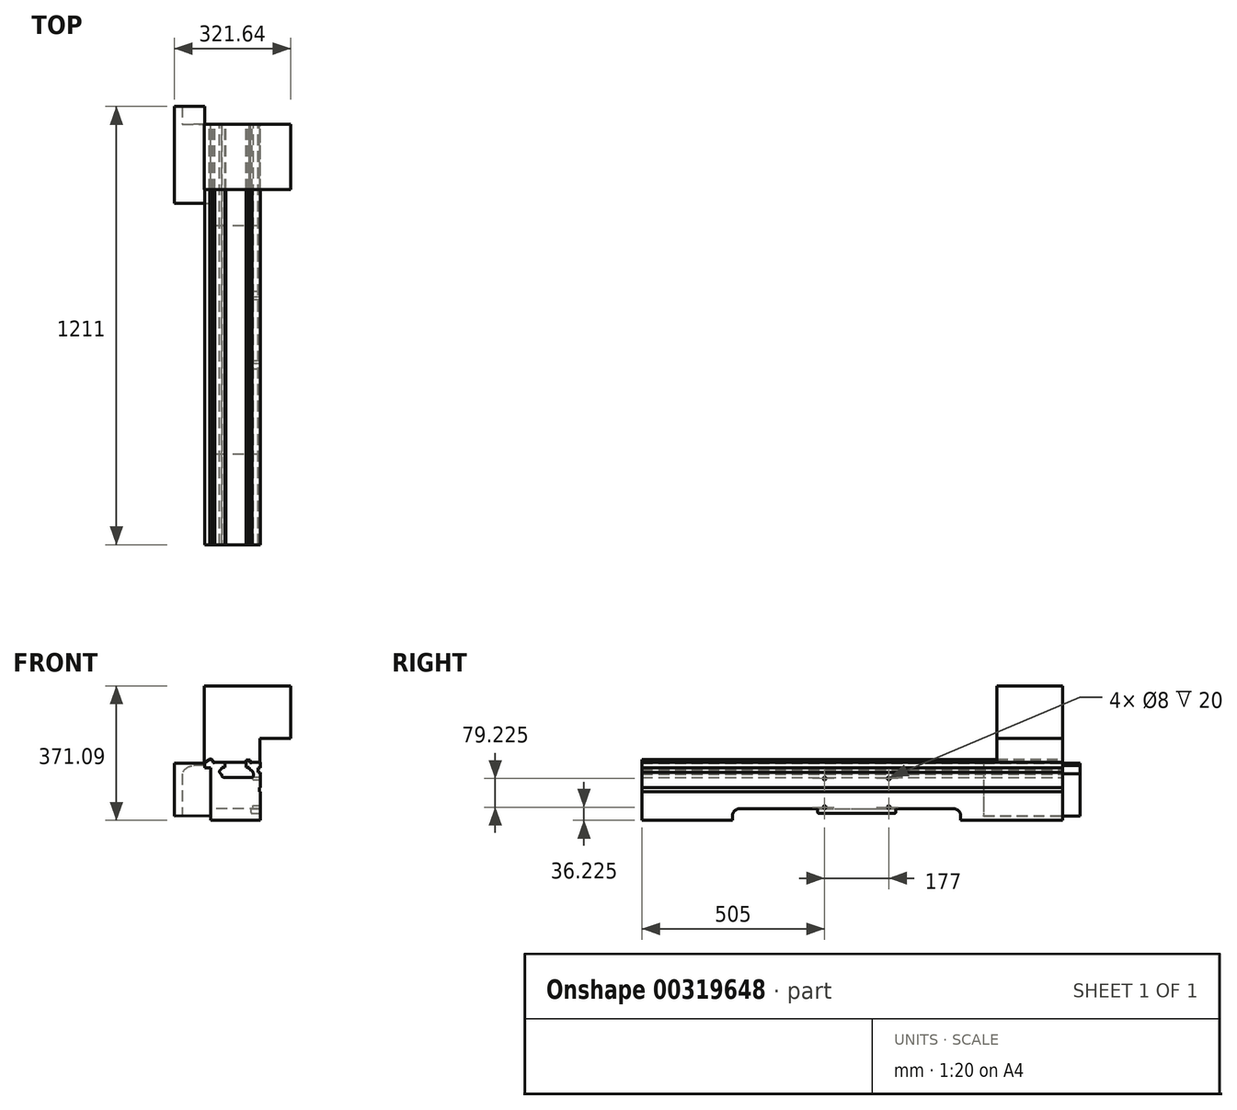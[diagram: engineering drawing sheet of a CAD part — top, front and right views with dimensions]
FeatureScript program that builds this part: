
annotation { "Feature Type Name" : "Feature", "Feature Type Description" : "" }
export const myFeature = defineFeature(function(context is Context, id is Id, definition is map)
    precondition{}
    {
        {
            var Q0;
            Q0=qCreatedBy(makeId("Front.planeOp"),FACE);
            var sketch = newSketch(context, id + "F0", { "sketchPlane" : qUnion([Q0])});
            skLineSegment(sketch, "E0", {"start": v(0, 0) * mm, "end": v(98, 0) * mm, "construction": true});
            skLineSegment(sketch, "E1", {"start": v(98, 0) * mm, "end": v(98, -15) * mm});
            skLineSegment(sketch, "E2", {"start": v(0, 0) * mm, "end": v(0, -14.5) * mm});
            skLineSegment(sketch, "E3", {"start": v(98, 0) * mm, "end": v(74.8, 0) * mm});
            skLineSegment(sketch, "E4", {"start": v(0, 0) * mm, "end": v(-27.25, 0) * mm});
            skLineSegment(sketch, "E5", {"start": v(0, 0) * mm, "end": v(-33, 0) * mm, "construction": true});
            skLineSegment(sketch, "E6.0", {"start": v(-33, -1.5) * mm, "end": v(98, -1.5) * mm, "construction": true});
            skLineSegment(sketch, "E7", {"start": v(-33, -1.5) * mm, "end": v(-33, 2) * mm});
            skLineSegment(sketch, "E8", {"start": v(-33, -1.5) * mm, "end": v(-29, -1.5) * mm});
            skLineSegment(sketch, "E9", {"start": v(98, -15) * mm, "end": v(58, -15) * mm, "construction": true});
            skLineSegment(sketch, "E10", {"start": v(0, -14.5) * mm, "end": v(-9, -14.5) * mm});
            skLineSegment(sketch, "E11", {"start": v(-9, -14.5) * mm, "end": v(-9, -19) * mm});
            skLineSegment(sketch, "E12", {"start": v(-27.25, 0) * mm, "end": v(-29, -1.5) * mm});
            skLineSegment(sketch, "E13", {"start": v(-33, 2) * mm, "end": v(-37.4, 7.44) * mm});
            skLineSegment(sketch, "E14", {"start": v(-37.4, 7.44) * mm, "end": v(-42.4, 7.44) * mm});
            skLineSegment(sketch, "E15", {"start": v(-42.4, 7.44) * mm, "end": v(-56.42, -2.19) * mm});
            skLineSegment(sketch, "E16", {"start": v(-56.42, -2.19) * mm, "end": v(-56.42, -15.19) * mm});
            skLineSegment(sketch, "E17", {"start": v(-56.42, -15.19) * mm, "end": v(-38.92, -15.19) * mm});
            skLineSegment(sketch, "E18", {"start": v(-38.92, -15.19) * mm, "end": v(-38.92, -97.19) * mm});
            skLineSegment(sketch, "E19", {"start": v(0, -14.5) * mm, "end": v(58, -14.5) * mm, "construction": true});
            skLineSegment(sketch, "E20", {"start": v(98, -15) * mm, "end": v(91.2, -15) * mm});
            skLineSegment(sketch, "E21", {"start": v(91.2, -15) * mm, "end": v(91.2, -28) * mm});
            skLineSegment(sketch, "E22", {"start": v(91.2, -28) * mm, "end": v(98, -28) * mm});
            skLineSegment(sketch, "E23", {"start": v(98, -28) * mm, "end": v(98, -70.45) * mm});
            skLineSegment(sketch, "E24", {"start": v(98, -70.45) * mm, "end": v(95.75, -70.45) * mm});
            skLineSegment(sketch, "E25", {"start": v(95.75, -70.45) * mm, "end": v(95.75, -80.95) * mm});
            skLineSegment(sketch, "E26", {"start": v(95.75, -80.95) * mm, "end": v(98, -80.95) * mm});
            skLineSegment(sketch, "E27", {"start": v(98, -80.95) * mm, "end": v(98, -160.45) * mm});
            skLineSegment(sketch, "E28", {"start": v(98, -160.45) * mm, "end": v(-38.92, -160.45) * mm});
            skLineSegment(sketch, "E29", {"start": v(-38.92, -160.45) * mm, "end": v(-38.92, -97.19) * mm});
            skLineSegment(sketch, "E30", {"start": v(68.7, -1.5) * mm, "end": v(68.7, 1) * mm});
            skLineSegment(sketch, "E31", {"start": v(68.7, -1.5) * mm, "end": v(72.95, -1.5) * mm});
            skLineSegment(sketch, "E32", {"start": v(72.95, -1.5) * mm, "end": v(74.8, 0) * mm});
            skLineSegment(sketch, "E33", {"start": v(68.7, 1) * mm, "end": v(65.56, 4.5) * mm});
            skLineSegment(sketch, "E34", {"start": v(65.56, 4.5) * mm, "end": v(61.71, 4.5) * mm});
            skLineSegment(sketch, "E35", {"start": v(61.71, 4.5) * mm, "end": v(58, 0.65) * mm});
            skLineSegment(sketch, "E36", {"start": v(58, 0.65) * mm, "end": v(58, -14.55) * mm});
            skLineSegment(sketch, "E37", {"start": v(58, -14.5) * mm, "end": v(68, -14.5) * mm});
            skLineSegment(sketch, "E38", {"start": v(68, -14.5) * mm, "end": v(68, -20.75) * mm});
            skLineSegment(sketch, "E39", {"start": v(2.3, -42) * mm, "end": v(71.25, -42) * mm});
            skArc(sketch, "E40", {"start": v(-9, -19) * mm, "mid": v(-15.02, -25.93) * mm, "end": v(-9, -32.86) * mm});
            skFitSpline(sketch, "E41", {"points": [v(-9, -32.86) * mm, v(-9, -37.28) * mm, v(-6.71, -40.5) * mm, v(-2.73, -41.64) * mm, v(0, -41.91) * mm, v(2.3, -42) * mm], "startDerivative": vector(-2.55, -20.76) * mm, "endDerivative": vector(16.47, -0.8) * mm});
            skFitSpline(sketch, "E42", {"points": [v(68, -20.75) * mm, v(72.98, -22.15) * mm, v(76.39, -26.46) * mm, v(78.72, -32.74) * mm, v(78.9, -37.4) * mm, v(77.64, -39.92) * mm, v(74.36, -41.44) * mm, v(71.25, -42) * mm], "startDerivative": vector(34.62, -4.93) * mm, "endDerivative": vector(-31.04, -3.2) * mm});
            skSolve(sketch);
        }
        {
            var Q0;
            Q0=makeQuery(id+"F0.imprint","IMPRINT",FACE,{"disambiguationData":[TD([[makeQuery(id+"F0.imprint","IMPRINT",EDGE,{"derivedFrom":sQuery(id+"F0.wireOp",EDGE,"E1")}),-1.0]])]});
            extrude(context, id + "F1", {"entities" : qUnion([Q0]), "depth" : 1162 * mm});
        }
        {
            var Q0;
            Q0=makeQuery(id+"F1.opExtrude","SWEPT_FACE",FACE,{"disambiguationData":[OSD([sQuery(id+"F0.wireOp",EDGE,"E18"),sQuery(id+"F0.wireOp",EDGE,"E29")])]});
            var sketch = newSketch(context, id + "F2", { "sketchPlane" : qUnion([Q0])});
            skLineSegment(sketch, "E43", {"start": v(1162, -160.45) * mm, "end": v(912, -160.45) * mm, "construction": true});
            skLineSegment(sketch, "E44", {"start": v(0, -160.45) * mm, "end": v(281, -160.45) * mm, "construction": true});
            skLineSegment(sketch, "E45", {"start": v(912, -160.45) * mm, "end": v(912, -148.45) * mm});
            skLineSegment(sketch, "E46", {"start": v(892, -128.45) * mm, "end": v(301, -128.45) * mm});
            skLineSegment(sketch, "E47", {"start": v(281, -148.45) * mm, "end": v(281, -160.45) * mm});
            skLineSegment(sketch, "E48", {"start": v(281, -160.45) * mm, "end": v(912, -160.45) * mm});
            skPoint(sketch, "E49.visualSharp", {"position": v(281, -128.45) * mm});
            skArc(sketch, "E49.filletArc", {"start": v(301, -128.45) * mm, "mid": v(286.86, -134.3) * mm, "end": v(281, -148.45) * mm});
            skPoint(sketch, "E50.visualSharp", {"position": v(912, -128.45) * mm});
            skArc(sketch, "E50.filletArc", {"start": v(912, -148.45) * mm, "mid": v(906.14, -134.3) * mm, "end": v(892, -128.45) * mm});
            skSolve(sketch);
        }
        {
            var Q0;
            Q0=makeQuery(id+"F2.imprint","IMPRINT",FACE,{"disambiguationData":[TD([[makeQuery(id+"F2.imprint","IMPRINT",EDGE,{"derivedFrom":sQuery(id+"F2.wireOp",EDGE,"E45")}),1.0]])]});
            var Q1;
            Q1=makeQuery(id+"F1.opExtrude","SWEPT_FACE",FACE,{"disambiguationData":[OSD([sQuery(id+"F0.wireOp",EDGE,"E27")])]});
            extrude(context, id + "F3", {"entities" : qUnion([Q0]), "operationType" : NewBodyOperationType.REMOVE, "endBound" : BoundingType.UP_TO_SURFACE, "oppositeDirection" : true, "endBoundEntityFace" : qUnion([Q1]), "depth" : 25 * mm});
        }
        {
            var Q0;
            Q0=makeQuery(id+"F1.opExtrude","SWEPT_FACE",FACE,{"disambiguationData":[OSD([sQuery(id+"F0.wireOp",EDGE,"E27")])]});
            var sketch = newSketch(context, id + "F4", { "sketchPlane" : qUnion([Q0])});
            skPoint(sketch, "E51.0", {"position": v(-1162, 0) * mm});
            skPoint(sketch, "E52.0", {"position": v(-1162, -160.45) * mm});
            skLineSegment(sketch, "E53", {"start": v(-673, -141.45) * mm, "end": v(-464, -141.45) * mm, "construction": true});
            skPoint(sketch, "E54.0", {"position": v(-1162, -28) * mm});
            skPoint(sketch, "E55.0", {"position": v(-1162, -70.45) * mm});
            skLineSegment(sketch, "E56", {"start": v(-1162, -28) * mm, "end": v(-1162, -70.45) * mm, "construction": true});
            skLineSegment(sketch, "E57", {"start": v(-657, -45) * mm, "end": v(-657, -141.45) * mm, "construction": true});
            skLineSegment(sketch, "E58", {"start": v(-480, -45) * mm, "end": v(-480, -141.45) * mm, "construction": true});
            skLineSegment(sketch, "E59", {"start": v(-657, -141.45) * mm, "end": v(-480, -141.45) * mm});
            skLineSegment(sketch, "E60", {"start": v(-676, -138.45) * mm, "end": v(-676, -128.45) * mm});
            skLineSegment(sketch, "E61", {"start": v(-676, -128.45) * mm, "end": v(-461, -128.45) * mm});
            skLineSegment(sketch, "E62", {"start": v(-461, -128.45) * mm, "end": v(-461, -138.45) * mm});
            skLineSegment(sketch, "E63", {"start": v(-676, -141.45) * mm, "end": v(-461, -141.45) * mm});
            skPoint(sketch, "E64.visualSharp", {"position": v(-676, -141.45) * mm});
            skArc(sketch, "E64.filletArc", {"start": v(-676, -138.45) * mm, "mid": v(-675.12, -140.57) * mm, "end": v(-673, -141.45) * mm});
            skPoint(sketch, "E65.visualSharp", {"position": v(-461, -141.45) * mm});
            skArc(sketch, "E65.filletArc", {"start": v(-464, -141.45) * mm, "mid": v(-461.88, -140.57) * mm, "end": v(-461, -138.45) * mm});
            skCircle(sketch, "E66", {"center": v(-657, -45) * mm, "radius": 4 * mm});
            skPoint(sketch, "E67", {"position": v(-657, -124.22) * mm});
            skLineSegment(sketch, "E68", {"start": v(-657, -45) * mm, "end": v(-480, -45) * mm, "construction": true});
            skLineSegment(sketch, "E69", {"start": v(-657, -124.22) * mm, "end": v(-480, -124.22) * mm, "construction": true});
            skCircle(sketch, "E70", {"center": v(-480, -45) * mm, "radius": 4 * mm});
            skCircle(sketch, "E71", {"center": v(-480, -124.22) * mm, "radius": 4 * mm});
            skCircle(sketch, "E72", {"center": v(-657, -124.22) * mm, "radius": 4 * mm});
            skLineSegment(sketch, "E73", {"start": v(-1162, -70.45) * mm, "end": v(-1162, -160.45) * mm, "construction": true});
            skSolve(sketch);
        }
        {
            var Q0;
            Q0=makeQuery(id+"F4.imprint","IMPRINT",FACE,{"disambiguationData":[TD([[makeQuery(id+"F4.imprint","IMPRINT",EDGE,{"derivedFrom":sQuery(id+"F4.wireOp",EDGE,"E60")}),-1.0]])]});
            extrude(context, id + "F5", {"entities" : qUnion([Q0]), "operationType" : NewBodyOperationType.ADD, "oppositeDirection" : true, "depth" : 25 * mm});
        }
        {
            var Q0;
            Q0=makeQuery(id+"F4.imprint","IMPRINT",FACE,{"disambiguationData":[TD([[makeQuery(id+"F4.imprint","IMPRINT",EDGE,{"derivedFrom":sQuery(id+"F4.wireOp",EDGE,"E66")}),1.0]])]});
            var Q1;
            Q1=makeQuery(id+"F4.imprint","IMPRINT",FACE,{"disambiguationData":[TD([[makeQuery(id+"F4.imprint","IMPRINT",EDGE,{"derivedFrom":sQuery(id+"F4.wireOp",EDGE,"E70")}),1.0]])]});
            var Q2;
            Q2=makeQuery(id+"F4.imprint","IMPRINT",FACE,{"disambiguationData":[TD([[makeQuery(id+"F4.imprint","IMPRINT",EDGE,{"derivedFrom":sQuery(id+"F4.wireOp",EDGE,"E71")}),1.0]])]});
            var Q3;
            Q3=makeQuery(id+"F4.imprint","IMPRINT",FACE,{"disambiguationData":[TD([[makeQuery(id+"F4.imprint","IMPRINT",EDGE,{"derivedFrom":sQuery(id+"F4.wireOp",EDGE,"E72")}),1.0]])]});
            extrude(context, id + "F6", {"entities" : qUnion([Q0, Q1, Q2, Q3]), "operationType" : NewBodyOperationType.REMOVE, "oppositeDirection" : true, "depth" : 20 * mm});
        }
        {
            var Q0;
            Q0=makeQuery(id+"F1.opExtrude","CAP_FACE",FACE,{"disambiguationData":[OSD([sQuery(id+"F0.wireOp",EDGE,"E1"),sQuery(id+"F0.wireOp",EDGE,"E2"),sQuery(id+"F0.wireOp",EDGE,"E3"),sQuery(id+"F0.wireOp",EDGE,"E4"),sQuery(id+"F0.wireOp",EDGE,"E7"),sQuery(id+"F0.wireOp",EDGE,"E8"),sQuery(id+"F0.wireOp",EDGE,"E10"),sQuery(id+"F0.wireOp",EDGE,"E11"),sQuery(id+"F0.wireOp",EDGE,"E12"),sQuery(id+"F0.wireOp",EDGE,"E13"),sQuery(id+"F0.wireOp",EDGE,"E14"),sQuery(id+"F0.wireOp",EDGE,"E15"),sQuery(id+"F0.wireOp",EDGE,"E16"),sQuery(id+"F0.wireOp",EDGE,"E17"),sQuery(id+"F0.wireOp",EDGE,"E18"),sQuery(id+"F0.wireOp",EDGE,"E20"),sQuery(id+"F0.wireOp",EDGE,"E21"),sQuery(id+"F0.wireOp",EDGE,"E22"),sQuery(id+"F0.wireOp",EDGE,"E23"),sQuery(id+"F0.wireOp",EDGE,"E24"),sQuery(id+"F0.wireOp",EDGE,"E25"),sQuery(id+"F0.wireOp",EDGE,"E26"),sQuery(id+"F0.wireOp",EDGE,"E27"),sQuery(id+"F0.wireOp",EDGE,"E28"),sQuery(id+"F0.wireOp",EDGE,"E29"),sQuery(id+"F0.wireOp",EDGE,"E30"),sQuery(id+"F0.wireOp",EDGE,"E31"),sQuery(id+"F0.wireOp",EDGE,"E32"),sQuery(id+"F0.wireOp",EDGE,"E33"),sQuery(id+"F0.wireOp",EDGE,"E34"),sQuery(id+"F0.wireOp",EDGE,"E35"),sQuery(id+"F0.wireOp",EDGE,"E36"),sQuery(id+"F0.wireOp",EDGE,"E37"),sQuery(id+"F0.wireOp",EDGE,"E38"),sQuery(id+"F0.wireOp",EDGE,"E39"),sQuery(id+"F0.wireOp",EDGE,"E40"),sQuery(id+"F0.wireOp",EDGE,"E41"),sQuery(id+"F0.wireOp",EDGE,"E42")])],"isStart":true});
            var sketch = newSketch(context, id + "F7", { "sketchPlane" : qUnion([Q0])});
            skLineSegment(sketch, "E74.0", {"start": v(56.42, -15.19) * mm, "end": v(38.92, -15.19) * mm});
            skLineSegment(sketch, "E75.0", {"start": v(56.42, -2.19) * mm, "end": v(56.42, -15.19) * mm});
            skLineSegment(sketch, "E76", {"start": v(56.42, -2.19) * mm, "end": v(139.62, -2.19) * mm});
            skLineSegment(sketch, "E77", {"start": v(139.62, -2.19) * mm, "end": v(139.62, -149.19) * mm});
            skLineSegment(sketch, "E78", {"start": v(139.62, -149.19) * mm, "end": v(38.92, -147.22) * mm});
            skLineSegment(sketch, "E79", {"start": v(38.92, -147.22) * mm, "end": v(38.92, -15.19) * mm});
            skLineSegment(sketch, "E80.0", {"start": v(118.02, -2.19) * mm, "end": v(118.02, -149.19) * mm});
            skPoint(sketch, "E81", {"position": v(91.42, -2.19) * mm});
            skLineSegment(sketch, "E82", {"start": v(91.42, -2.19) * mm, "end": v(91.42, -11.19) * mm});
            skPoint(sketch, "E83", {"position": v(56.42, -8.69) * mm});
            skLineSegment(sketch, "E84", {"start": v(56.42, -8.69) * mm, "end": v(91.42, -11.19) * mm});
            skPoint(sketch, "E85", {"position": v(118.02, -32.19) * mm});
            skArc(sketch, "E86", {"start": v(91.42, -11.19) * mm, "mid": v(107.95, -17.6) * mm, "end": v(118.02, -32.19) * mm});
            skSolve(sketch);
        }
        {
            var Q0;
            Q0=qSketchRegion(id+"F7",true);
            extrude(context, id + "F8", {"entities" : qUnion([Q0]), "oppositeDirection" : true, "depth" : 218 * mm});
        }
        {
            var Q0;
            {var subQ5=sQuery(id+"F7.wireOp",EDGE,"E77");Q0=makeQuery(id+"F7.imprint","IMPRINT",FACE,{"disambiguationData":[TD([[makeQuery(id+"F7.imprint","IMPRINT",EDGE,{"derivedFrom":subQ5}),-1.0]])]});}
            var Q1;
            {var subQ3=sQuery(id+"F7.wireOp",EDGE,"E82");Q1=makeQuery(id+"F7.imprint","IMPRINT",FACE,{"disambiguationData":[TD([[makeQuery(id+"F7.imprint","IMPRINT",EDGE,{"derivedFrom":subQ3}),1.0]])]});}
            var Q2;
            {var subQ4=sQuery(id+"F7.wireOp",EDGE,"E82");Q2=makeQuery(id+"F7.imprint","IMPRINT",FACE,{"disambiguationData":[TD([[makeQuery(id+"F7.imprint","IMPRINT",EDGE,{"derivedFrom":subQ4}),-1.0]])]});}
            extrude(context, id + "F9", {"entities" : qUnion([Q0, Q1, Q2]), "operationType" : NewBodyOperationType.ADD, "depth" : 49 * mm});
        }
        {
            var Q0;
            {var subQ6=sQuery(id+"F7.wireOp",EDGE,"E74.0");Q0=makeQuery(id+"F7.imprint","IMPRINT",FACE,{"disambiguationData":[TD([[makeQuery(id+"F7.imprint","IMPRINT",EDGE,{"derivedFrom":subQ6}),-1.0]])]});}
            var sketch = newSketch(context, id + "F10", { "sketchPlane" : qUnion([Q0])});
            skLineSegment(sketch, "E87.0", {"start": v(0, 0) * mm, "end": v(30.1, 0) * mm});
            skLineSegment(sketch, "E88.0", {"start": v(-96.02, 0) * mm, "end": v(-74.8, 0) * mm});
            skLineSegment(sketch, "E89.0", {"start": v(42.4, 7.44) * mm, "end": v(56.42, -2.19) * mm, "construction": true});
            skLineSegment(sketch, "E90.0", {"start": v(37.4, 7.44) * mm, "end": v(42.4, 7.44) * mm, "construction": true});
            skLineSegment(sketch, "E91.0", {"start": v(33, 2) * mm, "end": v(37.4, 7.44) * mm, "construction": true});
            skLineSegment(sketch, "E92.0", {"start": v(42.72, 8.44) * mm, "end": v(56.98, -1.36) * mm});
            skLineSegment(sketch, "E92.1", {"start": v(36.93, 8.44) * mm, "end": v(42.72, 8.44) * mm});
            skLineSegment(sketch, "E92.2", {"start": v(30.1, 0) * mm, "end": v(36.93, 8.44) * mm});
            skLineSegment(sketch, "E93.0", {"start": v(-65.56, 4.5) * mm, "end": v(-61.71, 4.5) * mm, "construction": true});
            skLineSegment(sketch, "E94.0", {"start": v(-68.7, 5.5) * mm, "end": v(-58, 5.5) * mm});
            skPoint(sketch, "E95.orphan", {"position": v(27.25, 0) * mm});
            skPoint(sketch, "E96.0", {"position": v(-58, 0.65) * mm});
            skLineSegment(sketch, "E97", {"start": v(0, 0) * mm, "end": v(-58, 0) * mm});
            skLineSegment(sketch, "E98", {"start": v(-58, 0) * mm, "end": v(-58, 0.65) * mm});
            skLineSegment(sketch, "E99", {"start": v(56.98, -1.36) * mm, "end": v(56.98, 210.64) * mm});
            skLineSegment(sketch, "E100", {"start": v(56.98, 210.64) * mm, "end": v(-182.02, 210.64) * mm});
            skLineSegment(sketch, "E101", {"start": v(-182.02, 210.64) * mm, "end": v(-182.02, 65.64) * mm});
            skLineSegment(sketch, "E102", {"start": v(-182.02, 65.64) * mm, "end": v(-96.02, 65.64) * mm});
            skLineSegment(sketch, "E103", {"start": v(-96.02, 65.64) * mm, "end": v(-96.02, 0) * mm});
            skPoint(sketch, "E104.orphan", {"position": v(-98, 0) * mm});
            skLineSegment(sketch, "E105", {"start": v(-58, 5.5) * mm, "end": v(-58, 0.65) * mm});
            skLineSegment(sketch, "E106", {"start": v(-74.8, 0) * mm, "end": v(-70.08, 0) * mm});
            skLineSegment(sketch, "E107", {"start": v(-70.08, 0) * mm, "end": v(-70.08, 5.5) * mm});
            skLineSegment(sketch, "E108", {"start": v(-70.08, 5.5) * mm, "end": v(-68.7, 5.5) * mm});
            skSolve(sketch);
        }
        {
            var Q0;
            Q0=makeQuery(id+"F10.imprint","IMPRINT",FACE,{"disambiguationData":[TD([[makeQuery(id+"F10.imprint","IMPRINT",EDGE,{"derivedFrom":sQuery(id+"F10.wireOp",EDGE,"E88.0")}),1.0]])]});
            extrude(context, id + "F11", {"entities" : qUnion([Q0]), "oppositeDirection" : true, "depth" : 181 * mm});
        }
    });
